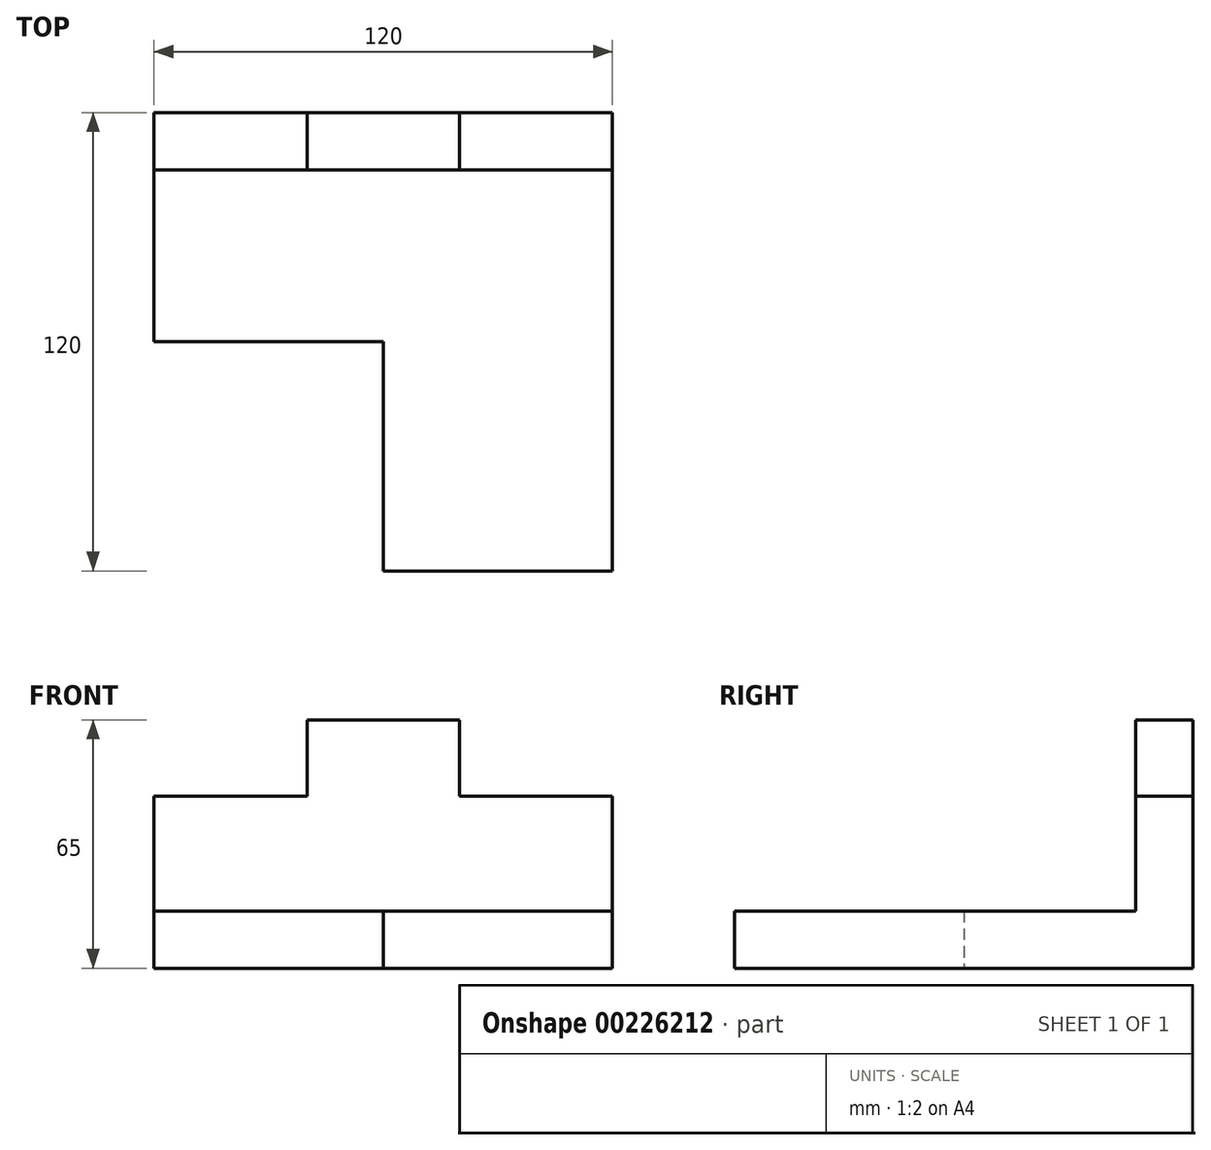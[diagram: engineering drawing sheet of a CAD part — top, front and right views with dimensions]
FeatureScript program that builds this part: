
annotation { "Feature Type Name" : "Feature", "Feature Type Description" : "" }
export const myFeature = defineFeature(function(context is Context, id is Id, definition is map)
    precondition{}
    {
        {
            var Q0;
            Q0=qCreatedBy(makeId("Top.planeOp"),FACE);
            var sketch = newSketch(context, id + "F0", { "sketchPlane" : qUnion([Q0])});
            skLineSegment(sketch, "E0.bottom", {"start": v(0, 0) * mm, "end": v(-120, 0) * mm});
            skLineSegment(sketch, "E0.top", {"start": v(0, -120) * mm, "end": v(-120, -120) * mm});
            skLineSegment(sketch, "E0.left", {"start": v(0, 0) * mm, "end": v(0, -120) * mm});
            skLineSegment(sketch, "E0.right", {"start": v(-120, 0) * mm, "end": v(-120, -120) * mm});
            skPoint(sketch, "E1.oppositeSnap0", {"position": v(-60, 0) * mm});
            skPoint(sketch, "E1.oppositeSnap1", {"position": v(0, -60) * mm});
            skLineSegment(sketch, "E1.bottom", {"start": v(-120, -120) * mm, "end": v(-60, -120) * mm});
            skLineSegment(sketch, "E1.top", {"start": v(-120, -60) * mm, "end": v(-60, -60) * mm});
            skLineSegment(sketch, "E1.left", {"start": v(-120, -120) * mm, "end": v(-120, -60) * mm});
            skLineSegment(sketch, "E1.right", {"start": v(-60, -120) * mm, "end": v(-60, -60) * mm});
            skSolve(sketch);
        }
        {
            var Q0;
            Q0=makeQuery(id+"F0.imprint","IMPRINT",FACE,{"disambiguationData":[TD([[makeQuery(id+"F0.imprint","IMPRINT",EDGE,{"derivedFrom":sQuery(id+"F0.wireOp",EDGE,"E0.bottom")}),1.0]])]});
            extrude(context, id + "F1", {"entities" : qUnion([Q0]), "depth" : 15 * mm});
        }
        {
            var Q0;
            Q0=makeQuery(id+"F1.opExtrude","SWEPT_FACE",FACE,{"disambiguationData":[OSD([sQuery(id+"F0.wireOp",EDGE,"E0.bottom")])]});
            var sketch = newSketch(context, id + "F2", { "sketchPlane" : qUnion([Q0])});
            skLineSegment(sketch, "E2.bottom", {"start": v(0, 0) * mm, "end": v(120, 0) * mm});
            skLineSegment(sketch, "E2.top", {"start": v(0, 65) * mm, "end": v(120, 65) * mm});
            skLineSegment(sketch, "E2.left", {"start": v(0, 0) * mm, "end": v(0, 65) * mm});
            skLineSegment(sketch, "E2.right", {"start": v(120, 0) * mm, "end": v(120, 65) * mm});
            skLineSegment(sketch, "E3.bottom", {"start": v(0, 65) * mm, "end": v(40, 65) * mm});
            skLineSegment(sketch, "E3.top", {"start": v(0, 45) * mm, "end": v(40, 45) * mm});
            skLineSegment(sketch, "E3.left", {"start": v(0, 65) * mm, "end": v(0, 45) * mm});
            skLineSegment(sketch, "E3.right", {"start": v(40, 65) * mm, "end": v(40, 45) * mm});
            skLineSegment(sketch, "E4", {"start": v(60, 65) * mm, "end": v(60, 0) * mm, "construction": true});
            skLineSegment(sketch, "E5.MirrorCS", {"start": v(80, 65) * mm, "end": v(80, 45) * mm});
            skLineSegment(sketch, "E6.MirrorCS", {"start": v(120, 45) * mm, "end": v(80, 45) * mm});
            skSolve(sketch);
        }
        {
            var Q0;
            {var subQ4=sQuery(id+"F2.wireOp",EDGE,"E3.top");Q0=makeQuery(id+"F2.imprint","IMPRINT",FACE,{"disambiguationData":[TD([[makeQuery(id+"F2.imprint","IMPRINT",EDGE,{"derivedFrom":subQ4}),-1.0]])]});}
            extrude(context, id + "F3", {"entities" : qUnion([Q0]), "operationType" : NewBodyOperationType.ADD, "oppositeDirection" : true, "depth" : 15 * mm});
        }
    });
